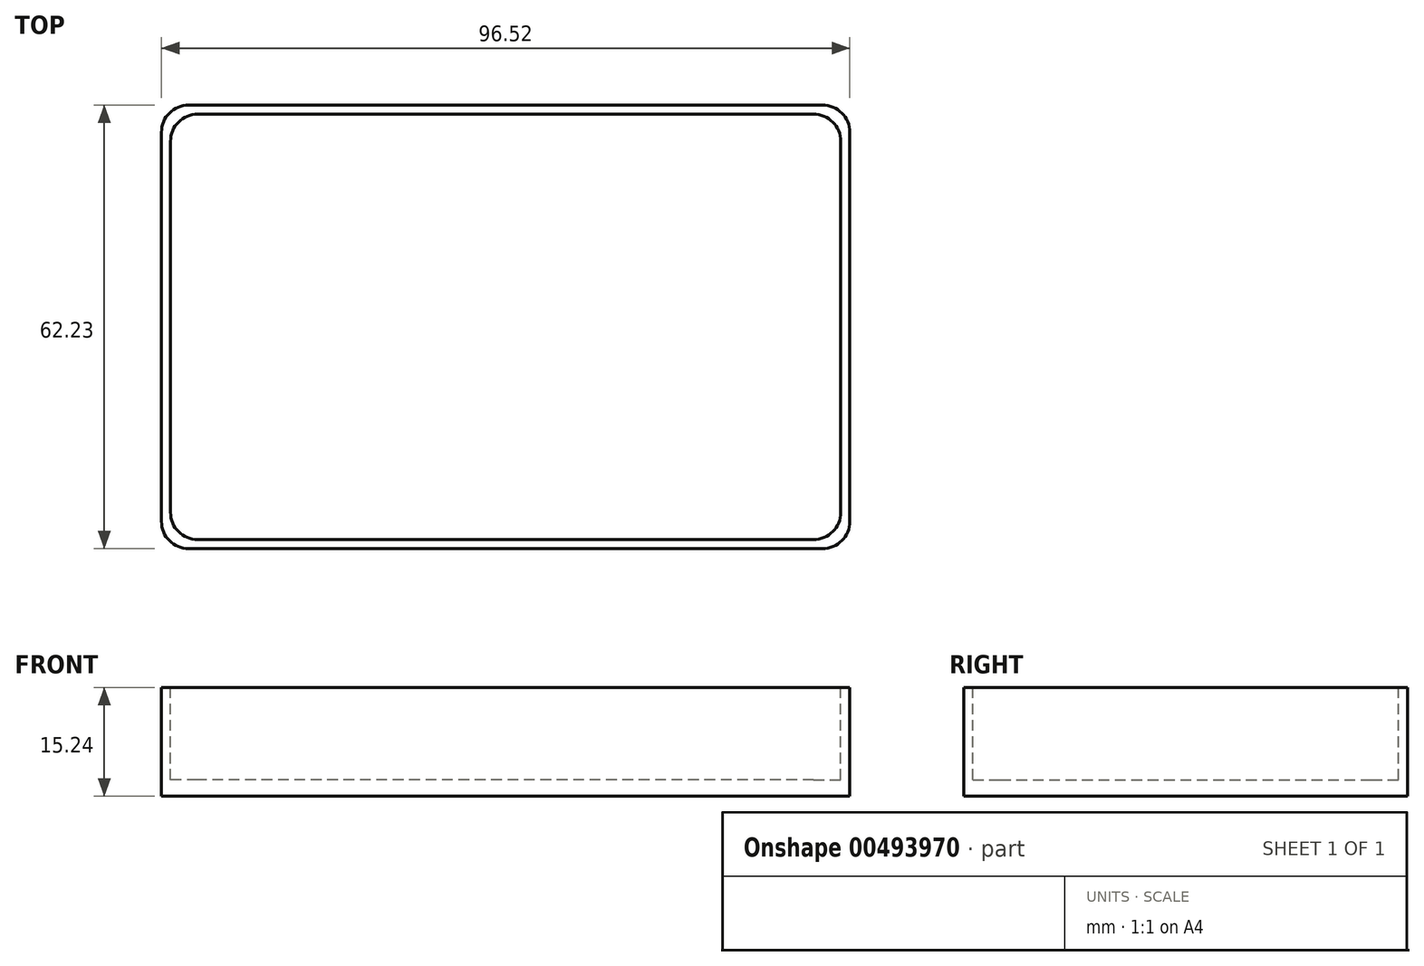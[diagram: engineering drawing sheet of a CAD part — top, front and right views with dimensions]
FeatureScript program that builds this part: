
annotation { "Feature Type Name" : "Feature", "Feature Type Description" : "" }
export const myFeature = defineFeature(function(context is Context, id is Id, definition is map)
    precondition{}
    {
        {
            var Q0;
            Q0=qCreatedBy(makeId("Top.planeOp"),FACE);
            var sketch = newSketch(context, id + "F0", { "sketchPlane" : qUnion([Q0])});
            skLineSegment(sketch, "E0.bottom", {"start": v(-18.92, 51.06) * mm, "end": v(77.6, 51.06) * mm});
            skLineSegment(sketch, "E0.top", {"start": v(-18.92, -11.17) * mm, "end": v(77.6, -11.17) * mm});
            skLineSegment(sketch, "E0.left", {"start": v(-18.92, 51.06) * mm, "end": v(-18.92, -11.17) * mm});
            skLineSegment(sketch, "E0.right", {"start": v(77.6, 51.06) * mm, "end": v(77.6, -11.17) * mm});
            skSolve(sketch);
        }
        {
            var Q0;
            Q0=makeQuery(id+"F0.imprint","IMPRINT",FACE,{"disambiguationData":[TD([[makeQuery(id+"F0.imprint","IMPRINT",EDGE,{"derivedFrom":sQuery(id+"F0.wireOp",EDGE,"E0.bottom")}),-1.0]])]});
            extrude(context, id + "F1", {"entities" : qUnion([Q0]), "depth" : 15.24 * mm});
        }
        {
            var Q0;
            Q0=makeQuery(id+"F1.opExtrude","SWEPT_EDGE",EDGE,{"disambiguationData":[OSD([sQuery(id+"F0.wireOp",EDGE,"E0.top"),sQuery(id+"F0.wireOp",EDGE,"E0.left")])]});
            fillet(context, id + "F2", {"entities" : qUnion([Q0]), "radius" : 3.8 * mm, "tangentPropagation" : true, "allowEdgeOverflow" : false});
        }
        {
            var Q0;
            Q0=makeQuery(id+"F1.opExtrude","SWEPT_EDGE",EDGE,{"disambiguationData":[OSD([sQuery(id+"F0.wireOp",EDGE,"E0.top"),sQuery(id+"F0.wireOp",EDGE,"E0.right")])]});
            fillet(context, id + "F3", {"entities" : qUnion([Q0]), "radius" : 3.8 * mm, "tangentPropagation" : true, "allowEdgeOverflow" : false});
        }
        {
            var Q0;
            Q0=makeQuery(id+"F1.opExtrude","SWEPT_EDGE",EDGE,{"disambiguationData":[OSD([sQuery(id+"F0.wireOp",EDGE,"E0.bottom"),sQuery(id+"F0.wireOp",EDGE,"E0.right")])]});
            fillet(context, id + "F4", {"entities" : qUnion([Q0]), "radius" : 3.8 * mm, "tangentPropagation" : true, "allowEdgeOverflow" : false});
        }
        {
            var Q0;
            Q0=makeQuery(id+"F1.opExtrude","SWEPT_EDGE",EDGE,{"disambiguationData":[OSD([sQuery(id+"F0.wireOp",EDGE,"E0.bottom"),sQuery(id+"F0.wireOp",EDGE,"E0.left")])]});
            fillet(context, id + "F5", {"entities" : qUnion([Q0]), "radius" : 3.8 * mm, "tangentPropagation" : true, "allowEdgeOverflow" : false});
        }
        {
            var Q0;
            Q0=makeQuery(id+"F1.opExtrude","CAP_FACE",FACE,{"disambiguationData":[OSD([sQuery(id+"F0.wireOp",EDGE,"E0.bottom"),sQuery(id+"F0.wireOp",EDGE,"E0.top"),sQuery(id+"F0.wireOp",EDGE,"E0.left"),sQuery(id+"F0.wireOp",EDGE,"E0.right")])],"isStart":false});
            var sketch = newSketch(context, id + "F6", { "sketchPlane" : qUnion([Q0])});
            skLineSegment(sketch, "E1.0", {"start": v(76.33, 49.79) * mm, "end": v(-17.65, 49.79) * mm});
            skLineSegment(sketch, "E1.1", {"start": v(76.33, -9.9) * mm, "end": v(76.33, 49.79) * mm});
            skLineSegment(sketch, "E1.2", {"start": v(-17.65, -9.9) * mm, "end": v(76.33, -9.9) * mm});
            skLineSegment(sketch, "E1.3", {"start": v(-17.65, 49.79) * mm, "end": v(-17.65, -9.9) * mm});
            skSolve(sketch);
        }
        {
            var Q0;
            Q0=makeQuery(id+"F6.imprint","IMPRINT",FACE,{"disambiguationData":[TD([[makeQuery(id+"F6.imprint","IMPRINT",EDGE,{"derivedFrom":sQuery(id+"F6.wireOp",EDGE,"E1.0")}),1.0]])]});
            extrude(context, id + "F7", {"entities" : qUnion([Q0]), "operationType" : NewBodyOperationType.REMOVE, "oppositeDirection" : true, "depth" : 12.95 * mm});
        }
        {
            var Q0;
            Q0=makeQuery(id+"F7.boolean.opBoolean","COPY",EDGE,{"derivedFrom":makeQuery(id+"F7.opExtrude","SWEPT_EDGE",EDGE,{"disambiguationData":[OSD([sQuery(id+"F6.wireOp",EDGE,"E1.0"),sQuery(id+"F6.wireOp",EDGE,"E1.3")])]})});
            fillet(context, id + "F8", {"entities" : qUnion([Q0]), "radius" : 3.8 * mm, "tangentPropagation" : true, "allowEdgeOverflow" : false});
        }
        {
            var Q0;
            Q0=makeQuery(id+"F7.boolean.opBoolean","COPY",EDGE,{"derivedFrom":makeQuery(id+"F7.opExtrude","SWEPT_EDGE",EDGE,{"disambiguationData":[OSD([sQuery(id+"F6.wireOp",EDGE,"E1.0"),sQuery(id+"F6.wireOp",EDGE,"E1.1")])]})});
            var Q1;
            Q1=makeQuery(id+"F7.boolean.opBoolean","COPY",EDGE,{"derivedFrom":makeQuery(id+"F7.opExtrude","SWEPT_EDGE",EDGE,{"disambiguationData":[OSD([sQuery(id+"F6.wireOp",EDGE,"E1.2"),sQuery(id+"F6.wireOp",EDGE,"E1.3")])]})});
            var Q2;
            Q2=makeQuery(id+"F7.boolean.opBoolean","COPY",EDGE,{"derivedFrom":makeQuery(id+"F7.opExtrude","SWEPT_EDGE",EDGE,{"disambiguationData":[OSD([sQuery(id+"F6.wireOp",EDGE,"E1.1"),sQuery(id+"F6.wireOp",EDGE,"E1.2")])]})});
            fillet(context, id + "F9", {"entities" : qUnion([Q0, Q1, Q2]), "radius" : 3.8 * mm, "tangentPropagation" : true, "allowEdgeOverflow" : false});
        }
    });
